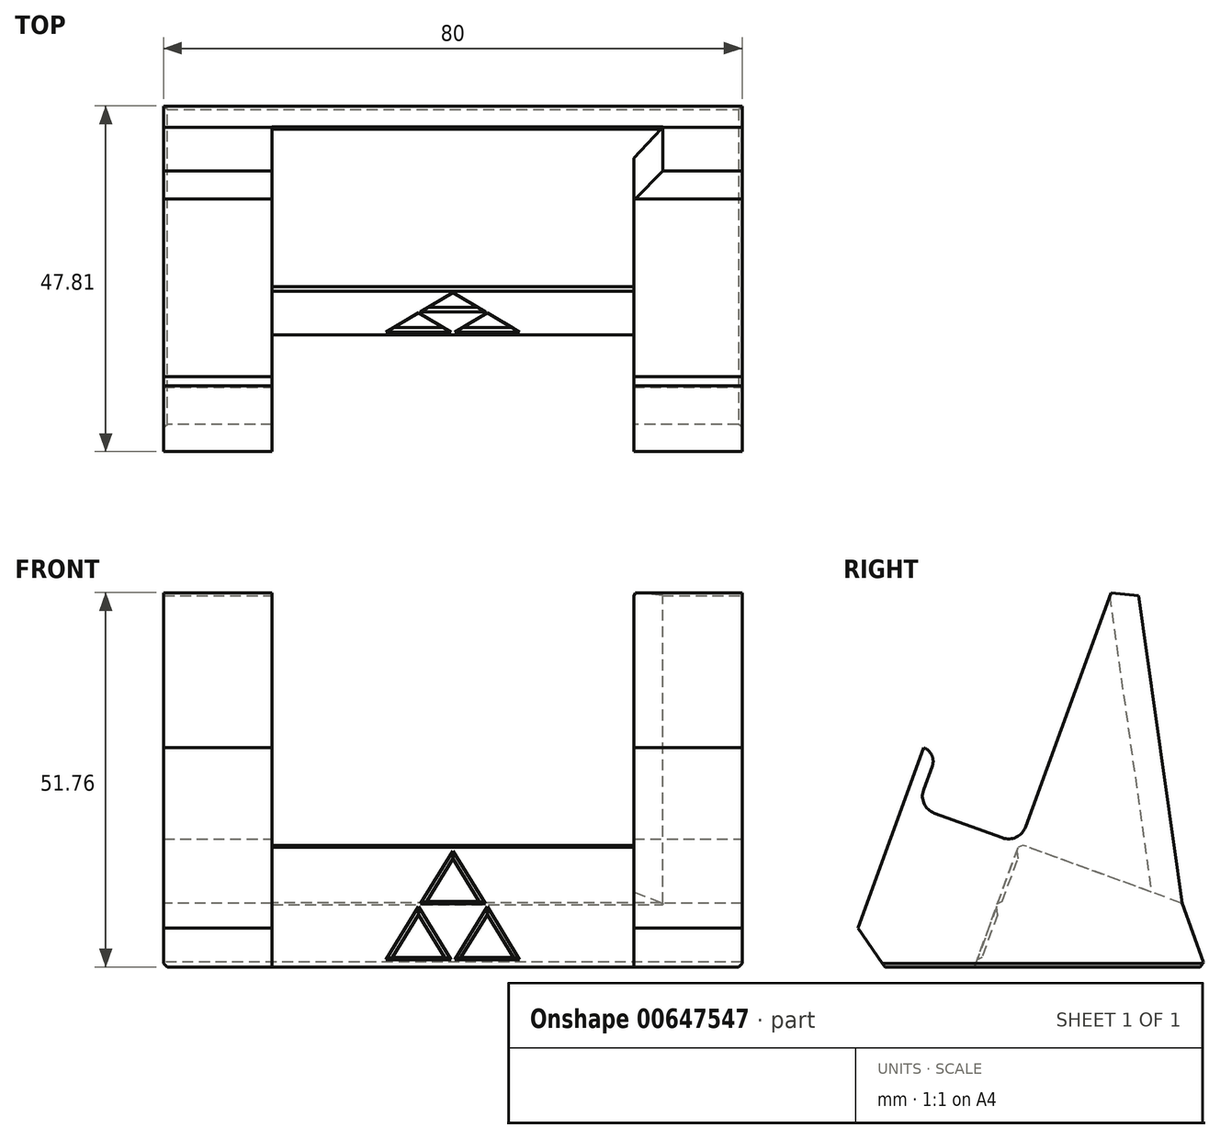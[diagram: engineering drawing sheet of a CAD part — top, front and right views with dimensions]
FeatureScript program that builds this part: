
annotation { "Feature Type Name" : "Feature", "Feature Type Description" : "" }
export const myFeature = defineFeature(function(context is Context, id is Id, definition is map)
    precondition{}
    {
        {
            var Q0;
            Q0=qCreatedBy(makeId("Top.planeOp"),FACE);
            var sketch = newSketch(context, id + "F0", { "sketchPlane" : qUnion([Q0])});
            skLineSegment(sketch, "E0.bottom", {"start": v(0, 0) * mm, "end": v(80, 0) * mm});
            skLineSegment(sketch, "E0.top", {"start": v(0, 50) * mm, "end": v(80, 50) * mm});
            skLineSegment(sketch, "E0.left", {"start": v(0, 0) * mm, "end": v(0, 50) * mm});
            skLineSegment(sketch, "E0.right", {"start": v(80, 0) * mm, "end": v(80, 50) * mm});
            skSolve(sketch);
        }
        {
            var Q0;
            Q0 = qSketchRegion(id + "F0", true);
            extrude(context, id + "F1", {"entities" : qUnion([Q0]), "depth" : 60 * mm, "offsetDistance" : 25 * mm});
        }
        {
            var Q0;
            Q0=makeQuery(id+"F1.opExtrude","SWEPT_FACE",FACE,{"disambiguationData":[OSD([sQuery(id+"F0.wireOp",EDGE,"E0.left")])]});
            var sketch = newSketch(context, id + "F2", { "sketchPlane" : qUnion([Q0])});
            skLineSegment(sketch, "E1", {"start": v(0, 0) * mm, "end": v(-11.04, 30.33) * mm});
            skLineSegment(sketch, "E2", {"start": v(-11.04, 30.33) * mm, "end": v(-12.92, 29.65) * mm});
            skLineSegment(sketch, "E3", {"start": v(-12.92, 29.65) * mm, "end": v(-10.18, 22.13) * mm});
            skLineSegment(sketch, "E4", {"start": v(-10.18, 22.13) * mm, "end": v(-24.28, 17) * mm});
            skLineSegment(sketch, "E5", {"start": v(-24.28, 17) * mm, "end": v(-39.67, 59.29) * mm});
            skLineSegment(sketch, "E6", {"start": v(-39.67, 59.29) * mm, "end": v(-46.8, 8.8) * mm});
            skLineSegment(sketch, "E7", {"start": v(-46.8, 8.8) * mm, "end": v(-50, 0) * mm});
            skLineSegment(sketch, "E8", {"start": v(-50, 0) * mm, "end": v(0, 0) * mm});
            skLineSegment(sketch, "E9", {"start": v(-50, 0) * mm, "end": v(-50, 60) * mm});
            skLineSegment(sketch, "E10", {"start": v(-50, 60) * mm, "end": v(0, 60) * mm});
            skLineSegment(sketch, "E11", {"start": v(0, 60) * mm, "end": v(0, 0) * mm});
            skLineSegment(sketch, "E12", {"start": v(-46.8, 8.8) * mm, "end": v(-10.18, 22.13) * mm, "construction": true});
            skSolve(sketch);
        }
        {
            var Q0;
            Q0=makeQuery(id+"F2.imprint","IMPRINT",FACE,{"disambiguationData":[TD([[makeQuery(id+"F2.imprint","IMPRINT",EDGE,{"derivedFrom":sQuery(id+"F2.wireOp",EDGE,"E1")}),-1.0]])]});
            var Q1;
            Q1=makeQuery(id+"F1.opExtrude","SWEPT_FACE",FACE,{"disambiguationData":[OSD([sQuery(id+"F0.wireOp",EDGE,"E0.right")])]});
            extrude(context, id + "F3", {"entities" : qUnion([Q0]), "operationType" : NewBodyOperationType.REMOVE, "endBound" : BoundingType.UP_TO_SURFACE, "oppositeDirection" : true, "depth" : 25 * mm, "endBoundEntityFace" : qUnion([Q1]), "offsetDistance" : 25 * mm});
        }
        {
            var Q0;
            Q0=makeQuery(id+"F3.boolean.opBoolean","COPY",FACE,{"derivedFrom":makeQuery(id+"F3.opExtrude","SWEPT_FACE",FACE,{"disambiguationData":[OSD([sQuery(id+"F2.wireOp",EDGE,"E5")])]})});
            var sketch = newSketch(context, id + "F4", { "sketchPlane" : qUnion([Q0])});
            skLineSegment(sketch, "E13", {"start": v(15, 69.28) * mm, "end": v(65, 69.28) * mm});
            skLineSegment(sketch, "E14", {"start": v(65, 69.28) * mm, "end": v(65, 24.28) * mm});
            skLineSegment(sketch, "E15", {"start": v(65, 24.28) * mm, "end": v(15, 24.28) * mm});
            skLineSegment(sketch, "E16", {"start": v(15, 24.28) * mm, "end": v(15, 69.28) * mm});
            skSolve(sketch);
        }
        {
            var Q0;
            Q0 = qSketchRegion(id + "F4", true);
            extrude(context, id + "F5", {"entities" : qUnion([Q0]), "operationType" : NewBodyOperationType.REMOVE, "endBound" : BoundingType.UP_TO_NEXT, "oppositeDirection" : true, "depth" : 25 * mm, "offsetDistance" : 25 * mm});
        }
        {
            var Q0;
            Q0=makeQuery(id+"F5.boolean.opBoolean","MERGE",FACE,{"derivedFrom":[makeQuery(id+"F3.boolean.opBoolean","COPY",FACE,{"derivedFrom":makeQuery(id+"F3.opExtrude","SWEPT_FACE",FACE,{"disambiguationData":[OSD([sQuery(id+"F2.wireOp",EDGE,"E4")])]})})],"fromTools":[makeQuery(id+"F5.opExtrude","SWEPT_FACE",FACE,{"disambiguationData":[OSD([sQuery(id+"F4.wireOp",EDGE,"E15")])]})]});
            var sketch = newSketch(context, id + "F6", { "sketchPlane" : qUnion([Q0])});
            skLineSegment(sketch, "E17", {"start": v(15, 17) * mm, "end": v(15, 0) * mm});
            skLineSegment(sketch, "E18", {"start": v(15, 17) * mm, "end": v(65, 17) * mm});
            skLineSegment(sketch, "E19", {"start": v(65, 17) * mm, "end": v(65, 0) * mm});
            skLineSegment(sketch, "E20", {"start": v(65, 0) * mm, "end": v(15, 0) * mm});
            skSolve(sketch);
        }
        {
            var Q0;
            Q0 = qSketchRegion(id + "F6", true);
            var Q1;
            Q1=makeQuery(id+"F1.opExtrude","CAP_FACE",FACE,{"disambiguationData":[OSD([sQuery(id+"F0.wireOp",EDGE,"E0.bottom"),sQuery(id+"F0.wireOp",EDGE,"E0.top"),sQuery(id+"F0.wireOp",EDGE,"E0.left"),sQuery(id+"F0.wireOp",EDGE,"E0.right")])],"isStart":true});
            var Q2;
            Q2=makeQuery(id+"F3.boolean.opBoolean","COPY",FACE,{"derivedFrom":makeQuery(id+"F3.opExtrude","SWEPT_FACE",FACE,{"disambiguationData":[OSD([sQuery(id+"F2.wireOp",EDGE,"E2")])]})});
            extrude(context, id + "F7", {"entities" : qUnion([Q0]), "operationType" : NewBodyOperationType.REMOVE, "endBound" : BoundingType.UP_TO_SURFACE, "oppositeDirection" : true, "depth" : 25 * mm, "endBoundEntityFace" : qUnion([Q1]), "offsetDistance" : 25 * mm, "hasSecondDirection" : true, "secondDirectionBound" : SecondDirectionBoundingType.UP_TO_SURFACE, "secondDirectionOppositeDirection" : false, "secondDirectionDepth" : 25 * mm, "secondDirectionBoundEntityFace" : qUnion([Q2])});
        }
        {
            var Q0;
            Q0=makeQuery(id+"F7.boolean.opBoolean","COPY",FACE,{"derivedFrom":makeQuery(id+"F7.opExtrude","SWEPT_FACE",FACE,{"disambiguationData":[OSD([sQuery(id+"F6.wireOp",EDGE,"E18")])]})});
            var sketch = newSketch(context, id + "F8", { "sketchPlane" : qUnion([Q0])});
            skLineSegment(sketch, "E21", {"start": v(40, 23.28) * mm, "end": v(40, 24.28) * mm, "construction": true});
            skLineSegment(sketch, "E22", {"start": v(40, 23.28) * mm, "end": v(35.5, 15.48) * mm});
            skLineSegment(sketch, "E23", {"start": v(35.5, 15.48) * mm, "end": v(44.5, 15.48) * mm});
            skLineSegment(sketch, "E24", {"start": v(44.5, 15.48) * mm, "end": v(40, 23.28) * mm});
            skLineSegment(sketch, "E25", {"start": v(30.75, 7.26) * mm, "end": v(39.75, 7.26) * mm});
            skLineSegment(sketch, "E26", {"start": v(35.25, 15.05) * mm, "end": v(30.75, 7.26) * mm});
            skLineSegment(sketch, "E27", {"start": v(35.25, 15.05) * mm, "end": v(39.75, 7.26) * mm});
            skLineSegment(sketch, "E28", {"start": v(40.25, 7.26) * mm, "end": v(44.75, 15.05) * mm});
            skLineSegment(sketch, "E29", {"start": v(44.75, 15.05) * mm, "end": v(49.25, 7.26) * mm});
            skLineSegment(sketch, "E30", {"start": v(49.25, 7.26) * mm, "end": v(40.25, 7.26) * mm});
            skLineSegment(sketch, "E31", {"start": v(30.75, 7.26) * mm, "end": v(40, 23.28) * mm, "construction": true});
            skLineSegment(sketch, "E32", {"start": v(40, 23.28) * mm, "end": v(49.25, 7.26) * mm, "construction": true});
            skSolve(sketch);
        }
        {
            var Q0;
            Q0 = qSketchRegion(id + "F8", true);
            extrude(context, id + "F9", {"entities" : qUnion([Q0]), "operationType" : NewBodyOperationType.REMOVE, "oppositeDirection" : true, "depth" : 0.5 * mm, "offsetDistance" : 25 * mm});
        }
        {
            var Q0;
            Q0=makeQuery(id+"F9.boolean.opBoolean","COPY",EDGE,{"derivedFrom":makeQuery(id+"F9.opExtrude","CAP_EDGE",EDGE,{"disambiguationData":[OSD([sQuery(id+"F8.wireOp",EDGE,"E22")])],"isStart":false})});
            var Q1;
            Q1=makeQuery(id+"F9.boolean.opBoolean","COPY",EDGE,{"derivedFrom":makeQuery(id+"F9.opExtrude","CAP_EDGE",EDGE,{"disambiguationData":[OSD([sQuery(id+"F8.wireOp",EDGE,"E24")])],"isStart":false})});
            var Q2;
            Q2=makeQuery(id+"F9.boolean.opBoolean","COPY",EDGE,{"derivedFrom":makeQuery(id+"F9.opExtrude","CAP_EDGE",EDGE,{"disambiguationData":[OSD([sQuery(id+"F8.wireOp",EDGE,"E23")])],"isStart":false})});
            var Q3;
            Q3=makeQuery(id+"F9.boolean.opBoolean","COPY",EDGE,{"derivedFrom":makeQuery(id+"F9.opExtrude","CAP_EDGE",EDGE,{"disambiguationData":[OSD([sQuery(id+"F8.wireOp",EDGE,"E27")])],"isStart":false})});
            var Q4;
            Q4=makeQuery(id+"F9.boolean.opBoolean","COPY",EDGE,{"derivedFrom":makeQuery(id+"F9.opExtrude","CAP_EDGE",EDGE,{"disambiguationData":[OSD([sQuery(id+"F8.wireOp",EDGE,"E28")])],"isStart":false})});
            var Q5;
            Q5=makeQuery(id+"F9.boolean.opBoolean","COPY",EDGE,{"derivedFrom":makeQuery(id+"F9.opExtrude","CAP_EDGE",EDGE,{"disambiguationData":[OSD([sQuery(id+"F8.wireOp",EDGE,"E26")])],"isStart":false})});
            var Q6;
            Q6=makeQuery(id+"F9.boolean.opBoolean","COPY",EDGE,{"derivedFrom":makeQuery(id+"F9.opExtrude","CAP_EDGE",EDGE,{"disambiguationData":[OSD([sQuery(id+"F8.wireOp",EDGE,"E25")])],"isStart":false})});
            var Q7;
            Q7=makeQuery(id+"F9.boolean.opBoolean","COPY",EDGE,{"derivedFrom":makeQuery(id+"F9.opExtrude","CAP_EDGE",EDGE,{"disambiguationData":[OSD([sQuery(id+"F8.wireOp",EDGE,"E30")])],"isStart":false})});
            var Q8;
            Q8=makeQuery(id+"F9.boolean.opBoolean","COPY",EDGE,{"derivedFrom":makeQuery(id+"F9.opExtrude","CAP_EDGE",EDGE,{"disambiguationData":[OSD([sQuery(id+"F8.wireOp",EDGE,"E29")])],"isStart":false})});
            chamfer(context, id + "F10", {"entities" : qUnion([Q0, Q1, Q2, Q3, Q4, Q5, Q6, Q7, Q8]), "width" : 0.5 * mm, "tangentPropagation" : true});
        }
        {
            var Q0;
            {var subQ0=sQuery(id+"F2.wireOp",EDGE,"E5");var subQ1=sQuery(id+"F2.wireOp",EDGE,"E4");Q0=makeQuery(id+"F5.boolean.opBoolean","SPLIT",EDGE,{"disambiguationData":[TD([makeQuery(id+"F1.opExtrude","SWEPT_FACE",FACE,{"disambiguationData":[OSD([sQuery(id+"F0.wireOp",EDGE,"E0.left")])]})])],"derivedFrom":makeQuery(id+"F3.boolean.opBoolean","COPY",EDGE,{"derivedFrom":makeQuery(id+"F3.opExtrude","SWEPT_EDGE",EDGE,{"disambiguationData":[OSD([subQ1,subQ0])]})})});}
            var Q1;
            {var subQ0=sQuery(id+"F2.wireOp",EDGE,"E3");var subQ1=sQuery(id+"F2.wireOp",EDGE,"E4");Q1=makeQuery(id+"F7.boolean.opBoolean","SPLIT",EDGE,{"disambiguationData":[TD([makeQuery(id+"F1.opExtrude","SWEPT_FACE",FACE,{"disambiguationData":[OSD([sQuery(id+"F0.wireOp",EDGE,"E0.left")])]})])],"derivedFrom":makeQuery(id+"F3.boolean.opBoolean","COPY",EDGE,{"derivedFrom":makeQuery(id+"F3.opExtrude","SWEPT_EDGE",EDGE,{"disambiguationData":[OSD([subQ0,subQ1])]})})});}
            var Q2;
            {var subQ0=sQuery(id+"F2.wireOp",EDGE,"E4");var subQ1=sQuery(id+"F2.wireOp",EDGE,"E5");Q2=makeQuery(id+"F5.boolean.opBoolean","SPLIT",EDGE,{"disambiguationData":[TD([makeQuery(id+"F1.opExtrude","SWEPT_FACE",FACE,{"disambiguationData":[OSD([sQuery(id+"F0.wireOp",EDGE,"E0.right")])]})])],"derivedFrom":makeQuery(id+"F3.boolean.opBoolean","COPY",EDGE,{"derivedFrom":makeQuery(id+"F3.opExtrude","SWEPT_EDGE",EDGE,{"disambiguationData":[OSD([subQ0,subQ1])]})})});}
            var Q3;
            {var subQ0=sQuery(id+"F2.wireOp",EDGE,"E3");var subQ1=sQuery(id+"F2.wireOp",EDGE,"E4");Q3=makeQuery(id+"F7.boolean.opBoolean","SPLIT",EDGE,{"disambiguationData":[TD([makeQuery(id+"F1.opExtrude","SWEPT_FACE",FACE,{"disambiguationData":[OSD([sQuery(id+"F0.wireOp",EDGE,"E0.right")])]})])],"derivedFrom":makeQuery(id+"F3.boolean.opBoolean","COPY",EDGE,{"derivedFrom":makeQuery(id+"F3.opExtrude","SWEPT_EDGE",EDGE,{"disambiguationData":[OSD([subQ0,subQ1])]})})});}
            fillet(context, id + "F11", {"entities" : qUnion([Q0, Q1, Q2, Q3]), "radius" : 2.5 * mm, "tangentPropagation" : true, "allowEdgeOverflow" : false});
        }
        {
            var Q0;
            {var subQ0=sQuery(id+"F2.wireOp",EDGE,"E2");var subQ1=sQuery(id+"F2.wireOp",EDGE,"E3");Q0=makeQuery(id+"F7.boolean.opBoolean","SPLIT",EDGE,{"disambiguationData":[TD([makeQuery(id+"F1.opExtrude","SWEPT_FACE",FACE,{"disambiguationData":[OSD([sQuery(id+"F0.wireOp",EDGE,"E0.left")])]})])],"derivedFrom":makeQuery(id+"F3.boolean.opBoolean","COPY",EDGE,{"derivedFrom":makeQuery(id+"F3.opExtrude","SWEPT_EDGE",EDGE,{"disambiguationData":[OSD([subQ0,subQ1])]})})});}
            var Q1;
            {var subQ0=sQuery(id+"F2.wireOp",EDGE,"E2");var subQ1=sQuery(id+"F2.wireOp",EDGE,"E3");Q1=makeQuery(id+"F7.boolean.opBoolean","SPLIT",EDGE,{"disambiguationData":[TD([makeQuery(id+"F1.opExtrude","SWEPT_FACE",FACE,{"disambiguationData":[OSD([sQuery(id+"F0.wireOp",EDGE,"E0.right")])]})])],"derivedFrom":makeQuery(id+"F3.boolean.opBoolean","COPY",EDGE,{"derivedFrom":makeQuery(id+"F3.opExtrude","SWEPT_EDGE",EDGE,{"disambiguationData":[OSD([subQ0,subQ1])]})})});}
            fillet(context, id + "F12", {"entities" : qUnion([Q0, Q1]), "radius" : 2 * mm, "tangentPropagation" : true, "allowEdgeOverflow" : false});
        }
        {
            var Q0;
            {var subQ0=sQuery(id+"F2.wireOp",EDGE,"E6");var subQ1=sQuery(id+"F2.wireOp",EDGE,"E5");Q0=makeQuery(id+"F5.boolean.opBoolean","SPLIT",EDGE,{"disambiguationData":[TD([makeQuery(id+"F1.opExtrude","SWEPT_FACE",FACE,{"disambiguationData":[OSD([sQuery(id+"F0.wireOp",EDGE,"E0.left")])]})])],"derivedFrom":makeQuery(id+"F3.boolean.opBoolean","COPY",EDGE,{"derivedFrom":makeQuery(id+"F3.opExtrude","SWEPT_EDGE",EDGE,{"disambiguationData":[OSD([subQ1,subQ0])]})})});}
            var Q1;
            {var subQ0=sQuery(id+"F2.wireOp",EDGE,"E5");var subQ1=sQuery(id+"F2.wireOp",EDGE,"E6");Q1=makeQuery(id+"F5.boolean.opBoolean","SPLIT",EDGE,{"disambiguationData":[TD([makeQuery(id+"F1.opExtrude","SWEPT_FACE",FACE,{"disambiguationData":[OSD([sQuery(id+"F0.wireOp",EDGE,"E0.right")])]})])],"derivedFrom":makeQuery(id+"F3.boolean.opBoolean","COPY",EDGE,{"derivedFrom":makeQuery(id+"F3.opExtrude","SWEPT_EDGE",EDGE,{"disambiguationData":[OSD([subQ0,subQ1])]})})});}
            chamfer(context, id + "F13", {"entities" : qUnion([Q0, Q1]), "width" : 2 * mm, "tangentPropagation" : true});
        }
        {
            var Q0;
            Q0=makeQuery(id+"F3.boolean.opBoolean","COPY",EDGE,{"derivedFrom":makeQuery(id+"F3.opExtrude","CAP_EDGE",EDGE,{"disambiguationData":[OSD([sQuery(id+"F2.wireOp",EDGE,"E1")])],"isStart":true})});
            var Q1;
            {var subQ0=sQuery(id+"F6.wireOp",EDGE,"E20");var subQ1=sQuery(id+"F6.wireOp",EDGE,"E17");var subQ2=sQuery(id+"F2.wireOp",EDGE,"E4");var subQ3=makeQuery(id+"F6.imprint","INTERSECT",VERTEX,{"derivedFrom":[makeQuery(id+"F3.boolean.opBoolean","COPY",EDGE,{"derivedFrom":makeQuery(id+"F3.opExtrude","SWEPT_EDGE",EDGE,{"disambiguationData":[OSD([sQuery(id+"F2.wireOp",EDGE,"E3"),subQ2])]})}),subQ1]});Q1=makeQuery(id+"F7.boolean.opBoolean","COPY",EDGE,{"derivedFrom":makeQuery(id+"F7.opExtrude","TWEAK_EDGE",EDGE,{"derivedFrom":[makeQuery(id+"F6.imprint","IMPRINT",EDGE,{"disambiguationData":[TD([[subQ3,1.0]])],"derivedFrom":subQ1}),makeQuery(id+"F6.imprint","IMPRINT",EDGE,{"disambiguationData":[TD([[makeQuery(id+"F6.imprint","INTERSECT",VERTEX,{"derivedFrom":[subQ1,subQ0]}),1.0]])],"derivedFrom":subQ1}),makeQuery(id+"F6.imprint","IMPRINT",EDGE,{"derivedFrom":subQ0})]})});}
            var Q2;
            {var subQ0=sQuery(id+"F6.wireOp",EDGE,"E20");var subQ1=sQuery(id+"F6.wireOp",EDGE,"E19");var subQ2=sQuery(id+"F2.wireOp",EDGE,"E4");var subQ3=makeQuery(id+"F6.imprint","INTERSECT",VERTEX,{"derivedFrom":[makeQuery(id+"F3.boolean.opBoolean","COPY",EDGE,{"derivedFrom":makeQuery(id+"F3.opExtrude","SWEPT_EDGE",EDGE,{"disambiguationData":[OSD([sQuery(id+"F2.wireOp",EDGE,"E3"),subQ2])]})}),subQ1]});Q2=makeQuery(id+"F7.boolean.opBoolean","COPY",EDGE,{"derivedFrom":makeQuery(id+"F7.opExtrude","TWEAK_EDGE",EDGE,{"derivedFrom":[makeQuery(id+"F6.imprint","IMPRINT",EDGE,{"disambiguationData":[TD([[subQ3,1.0]])],"derivedFrom":subQ1}),makeQuery(id+"F6.imprint","IMPRINT",EDGE,{"disambiguationData":[TD([[makeQuery(id+"F6.imprint","INTERSECT",VERTEX,{"derivedFrom":[subQ1,subQ0]}),1.0]])],"derivedFrom":subQ1}),makeQuery(id+"F6.imprint","IMPRINT",EDGE,{"derivedFrom":subQ0})]})});}
            var Q3;
            Q3=makeQuery(id+"F3.boolean.opBoolean","COPY",EDGE,{"derivedFrom":makeQuery(id+"F3.opExtrude","CAP_EDGE",EDGE,{"disambiguationData":[OSD([sQuery(id+"F2.wireOp",EDGE,"E1")])],"isStart":false})});
            var Q4;
            {var subQ0=sQuery(id+"F0.wireOp",EDGE,"E0.left");var subQ1=sQuery(id+"F0.wireOp",EDGE,"E0.bottom");var subQ2=sQuery(id+"F2.wireOp",EDGE,"E1");Q4=makeQuery(id+"F7.boolean.opBoolean","SPLIT",EDGE,{"disambiguationData":[TD([makeQuery(id+"F1.opExtrude","SWEPT_FACE",FACE,{"disambiguationData":[OSD([subQ0])]})])],"derivedFrom":makeQuery(id+"F3.boolean.opBoolean","MERGE",EDGE,{"derivedFrom":[makeQuery(id+"F1.opExtrude","CAP_EDGE",EDGE,{"disambiguationData":[OSD([subQ1])],"isStart":true})],"fromTools":[makeQuery(id+"F3.opExtrude","SWEPT_EDGE",EDGE,{"disambiguationData":[OSD([subQ2,sQuery(id+"F2.wireOp",EDGE,"E8"),sQuery(id+"F2.wireOp",EDGE,"E11")])]})]})});}
            var Q5;
            {var subQ0=sQuery(id+"F0.wireOp",EDGE,"E0.right");var subQ1=sQuery(id+"F0.wireOp",EDGE,"E0.bottom");var subQ2=sQuery(id+"F2.wireOp",EDGE,"E1");Q5=makeQuery(id+"F7.boolean.opBoolean","SPLIT",EDGE,{"disambiguationData":[TD([makeQuery(id+"F1.opExtrude","SWEPT_FACE",FACE,{"disambiguationData":[OSD([subQ0])]})])],"derivedFrom":makeQuery(id+"F3.boolean.opBoolean","MERGE",EDGE,{"derivedFrom":[makeQuery(id+"F1.opExtrude","CAP_EDGE",EDGE,{"disambiguationData":[OSD([subQ1])],"isStart":true})],"fromTools":[makeQuery(id+"F3.opExtrude","SWEPT_EDGE",EDGE,{"disambiguationData":[OSD([subQ2,sQuery(id+"F2.wireOp",EDGE,"E8"),sQuery(id+"F2.wireOp",EDGE,"E11")])]})]})});}
            var Q6;
            Q6=makeQuery(id+"F3.boolean.opBoolean","COPY",EDGE,{"derivedFrom":makeQuery(id+"F3.opExtrude","CAP_EDGE",EDGE,{"disambiguationData":[OSD([sQuery(id+"F2.wireOp",EDGE,"E6")])],"isStart":false})});
            var Q7;
            Q7=makeQuery(id+"F3.boolean.opBoolean","COPY",EDGE,{"derivedFrom":makeQuery(id+"F3.opExtrude","CAP_EDGE",EDGE,{"disambiguationData":[OSD([sQuery(id+"F2.wireOp",EDGE,"E7")])],"isStart":false})});
            var Q8;
            Q8=makeQuery(id+"F3.boolean.opBoolean","COPY",EDGE,{"derivedFrom":makeQuery(id+"F3.opExtrude","CAP_EDGE",EDGE,{"disambiguationData":[OSD([sQuery(id+"F2.wireOp",EDGE,"E7")])],"isStart":true})});
            var Q9;
            Q9=makeQuery(id+"F3.boolean.opBoolean","COPY",EDGE,{"derivedFrom":makeQuery(id+"F3.opExtrude","CAP_EDGE",EDGE,{"disambiguationData":[OSD([sQuery(id+"F2.wireOp",EDGE,"E6")])],"isStart":true})});
            var Q10;
            Q10=makeQuery(id+"F5.boolean.opBoolean","COPY",EDGE,{"derivedFrom":makeQuery(id+"F5.opExtrude","TWEAK_EDGE",EDGE,{"derivedFrom":[makeQuery(id+"F3.boolean.opBoolean","COPY",FACE,{"derivedFrom":makeQuery(id+"F3.opExtrude","SWEPT_FACE",FACE,{"disambiguationData":[OSD([sQuery(id+"F2.wireOp",EDGE,"E6")])]})}),makeQuery(id+"F4.imprint","IMPRINT",EDGE,{"derivedFrom":sQuery(id+"F4.wireOp",EDGE,"E16")})]})});
            var Q11;
            Q11=makeQuery(id+"F5.boolean.opBoolean","COPY",EDGE,{"derivedFrom":makeQuery(id+"F5.opExtrude","TWEAK_EDGE",EDGE,{"derivedFrom":[makeQuery(id+"F3.boolean.opBoolean","COPY",FACE,{"derivedFrom":makeQuery(id+"F3.opExtrude","SWEPT_FACE",FACE,{"disambiguationData":[OSD([sQuery(id+"F2.wireOp",EDGE,"E6")])]})}),makeQuery(id+"F4.imprint","IMPRINT",EDGE,{"derivedFrom":sQuery(id+"F4.wireOp",EDGE,"E14")})]})});
            chamfer(context, id + "F14", {"entities" : qUnion([Q0, Q1, Q2, Q3, Q4, Q5, Q6, Q7, Q8, Q9, Q10, Q11]), "width" : 4 * mm, "tangentPropagation" : true});
        }
        {
            var Q0;
            Q0=makeQuery(id+"F1.opExtrude","CAP_EDGE",EDGE,{"disambiguationData":[OSD([sQuery(id+"F0.wireOp",EDGE,"E0.right")])],"isStart":true});
            var Q1;
            Q1=makeQuery(id+"F14.opChamfer","BLEND_EDGE",EDGE,{"blendedFrom":[makeQuery(id+"F3.boolean.opBoolean","COPY",EDGE,{"derivedFrom":makeQuery(id+"F3.opExtrude","CAP_EDGE",EDGE,{"disambiguationData":[OSD([sQuery(id+"F2.wireOp",EDGE,"E7")])],"isStart":false})}),makeQuery(id+"F1.opExtrude","CAP_FACE",FACE,{"disambiguationData":[OSD([sQuery(id+"F0.wireOp",EDGE,"E0.bottom"),sQuery(id+"F0.wireOp",EDGE,"E0.top"),sQuery(id+"F0.wireOp",EDGE,"E0.left"),sQuery(id+"F0.wireOp",EDGE,"E0.right")])],"isStart":true})],"blendedInto":[makeQuery(id+"F1.opExtrude","CAP_FACE",FACE,{"disambiguationData":[OSD([sQuery(id+"F0.wireOp",EDGE,"E0.bottom"),sQuery(id+"F0.wireOp",EDGE,"E0.top"),sQuery(id+"F0.wireOp",EDGE,"E0.left"),sQuery(id+"F0.wireOp",EDGE,"E0.right")])],"isStart":true})]});
            var Q2;
            Q2=makeQuery(id+"F3.boolean.opBoolean","MERGE",EDGE,{"derivedFrom":[makeQuery(id+"F1.opExtrude","CAP_EDGE",EDGE,{"disambiguationData":[OSD([sQuery(id+"F0.wireOp",EDGE,"E0.top")])],"isStart":true})],"fromTools":[makeQuery(id+"F3.opExtrude","SWEPT_EDGE",EDGE,{"disambiguationData":[OSD([sQuery(id+"F2.wireOp",EDGE,"E7"),sQuery(id+"F2.wireOp",EDGE,"E8"),sQuery(id+"F2.wireOp",EDGE,"E9")])]})]});
            var Q3;
            Q3=makeQuery(id+"F14.opChamfer","BLEND_EDGE",EDGE,{"blendedFrom":[makeQuery(id+"F3.boolean.opBoolean","COPY",EDGE,{"derivedFrom":makeQuery(id+"F3.opExtrude","CAP_EDGE",EDGE,{"disambiguationData":[OSD([sQuery(id+"F2.wireOp",EDGE,"E7")])],"isStart":true})}),makeQuery(id+"F1.opExtrude","CAP_FACE",FACE,{"disambiguationData":[OSD([sQuery(id+"F0.wireOp",EDGE,"E0.bottom"),sQuery(id+"F0.wireOp",EDGE,"E0.top"),sQuery(id+"F0.wireOp",EDGE,"E0.left"),sQuery(id+"F0.wireOp",EDGE,"E0.right")])],"isStart":true})],"blendedInto":[makeQuery(id+"F1.opExtrude","CAP_FACE",FACE,{"disambiguationData":[OSD([sQuery(id+"F0.wireOp",EDGE,"E0.bottom"),sQuery(id+"F0.wireOp",EDGE,"E0.top"),sQuery(id+"F0.wireOp",EDGE,"E0.left"),sQuery(id+"F0.wireOp",EDGE,"E0.right")])],"isStart":true})]});
            var Q4;
            Q4=makeQuery(id+"F1.opExtrude","CAP_EDGE",EDGE,{"disambiguationData":[OSD([sQuery(id+"F0.wireOp",EDGE,"E0.left")])],"isStart":true});
            var Q5;
            Q5=makeQuery(id+"F7.boolean.opBoolean","COPY",EDGE,{"derivedFrom":makeQuery(id+"F7.opExtrude","CAP_EDGE",EDGE,{"disambiguationData":[OSD([sQuery(id+"F6.wireOp",EDGE,"E19")])],"isStart":false})});
            var Q6;
            Q6=makeQuery(id+"F7.boolean.opBoolean","COPY",EDGE,{"derivedFrom":makeQuery(id+"F7.opExtrude","CAP_EDGE",EDGE,{"disambiguationData":[OSD([sQuery(id+"F6.wireOp",EDGE,"E17")])],"isStart":false})});
            var Q7;
            Q7=makeQuery(id+"F7.boolean.opBoolean","INTERSECT",EDGE,{"derivedFrom":[makeQuery(id+"F5.boolean.opBoolean","MERGE",FACE,{"derivedFrom":[makeQuery(id+"F3.boolean.opBoolean","COPY",FACE,{"derivedFrom":makeQuery(id+"F3.opExtrude","SWEPT_FACE",FACE,{"disambiguationData":[OSD([sQuery(id+"F2.wireOp",EDGE,"E4")])]})})],"fromTools":[makeQuery(id+"F5.opExtrude","SWEPT_FACE",FACE,{"disambiguationData":[OSD([sQuery(id+"F4.wireOp",EDGE,"E15")])]})]}),makeQuery(id+"F7.opExtrude","SWEPT_FACE",FACE,{"disambiguationData":[OSD([sQuery(id+"F6.wireOp",EDGE,"E18")])]})]});
            var Q8;
            Q8=makeQuery(id+"F5.boolean.opBoolean","MERGE",EDGE,{"derivedFrom":[makeQuery(id+"F3.boolean.opBoolean","COPY",EDGE,{"derivedFrom":makeQuery(id+"F3.opExtrude","SWEPT_EDGE",EDGE,{"disambiguationData":[OSD([sQuery(id+"F2.wireOp",EDGE,"E6"),sQuery(id+"F2.wireOp",EDGE,"E7")])]})})],"fromTools":[makeQuery(id+"F5.opExtrude","CAP_EDGE",EDGE,{"disambiguationData":[OSD([sQuery(id+"F4.wireOp",EDGE,"E15")])],"isStart":false})]});
            chamfer(context, id + "F15", {"entities" : qUnion([Q0, Q1, Q2, Q3, Q4, Q5, Q6, Q7, Q8]), "width" : 0.5 * mm, "tangentPropagation" : true});
        }
    });
